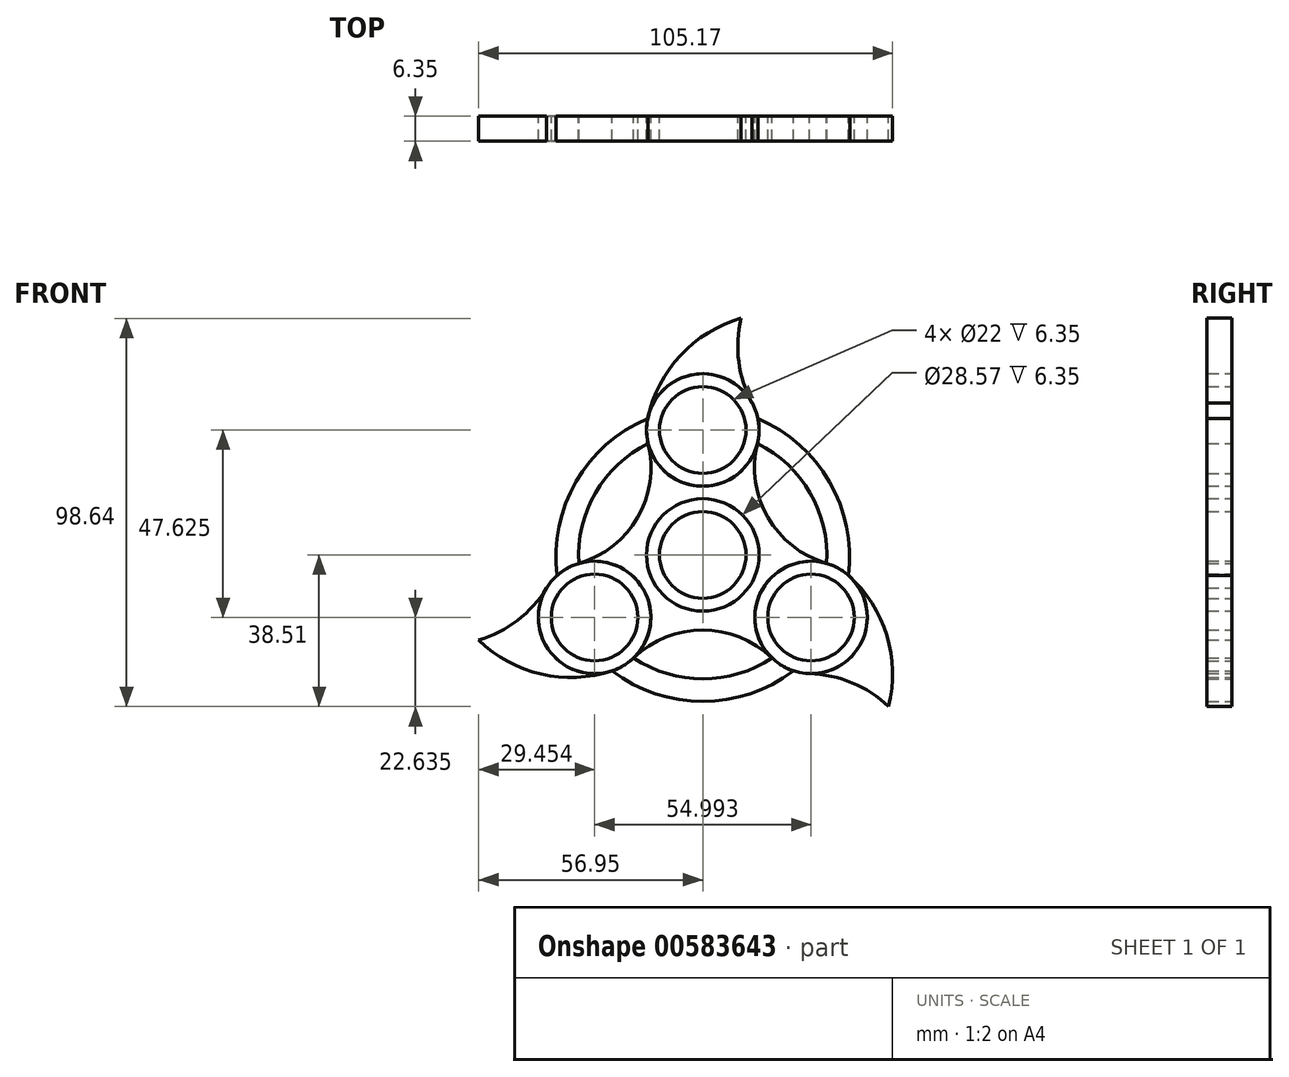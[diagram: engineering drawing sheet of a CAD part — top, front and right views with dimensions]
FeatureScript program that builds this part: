
annotation { "Feature Type Name" : "Feature", "Feature Type Description" : "" }
export const myFeature = defineFeature(function(context is Context, id is Id, definition is map)
    precondition{}
    {
        {
            var Q0;
            Q0=qCreatedBy(makeId("Front.planeOp"),FACE);
            var sketch = newSketch(context, id + "F0", { "sketchPlane" : qUnion([Q0])});
            skCircle(sketch, "E0", {"center": v(0, 0) * mm, "radius": 14.29 * mm});
            skCircle(sketch, "E1", {"center": v(0, 0) * mm, "radius": 11 * mm});
            skCircle(sketch, "E2", {"center": v(0, 31.75) * mm, "radius": 14.29 * mm});
            skCircle(sketch, "E3", {"center": v(0, 31.75) * mm, "radius": 11 * mm});
            skCircle(sketch, "E4.1.0", {"center": v(-27.5, -15.87) * mm, "radius": 11 * mm});
            skCircle(sketch, "E4.1.1", {"center": v(-27.5, -15.87) * mm, "radius": 14.29 * mm});
            skCircle(sketch, "E4.2.0", {"center": v(27.5, -15.88) * mm, "radius": 11 * mm});
            skCircle(sketch, "E4.2.1", {"center": v(27.5, -15.88) * mm, "radius": 14.29 * mm});
            skSolve(sketch);
        }
        {
            var Q0;
            Q0=qCreatedBy(makeId("Front.planeOp"),FACE);
            var sketch = newSketch(context, id + "F1", { "sketchPlane" : qUnion([Q0])});
            skCircle(sketch, "E5.0", {"center": v(0, 31.75) * mm, "radius": 14.29 * mm});
            skCircle(sketch, "E6.0", {"center": v(27.5, -15.88) * mm, "radius": 14.29 * mm});
            skCircle(sketch, "E7.0", {"center": v(-27.5, -15.87) * mm, "radius": 14.29 * mm});
            skCircle(sketch, "E8.0", {"center": v(0, 0) * mm, "radius": 14.29 * mm});
            skArc(sketch, "E9", {"start": v(-31.47, -2.15) * mm, "mid": v(-16.54, 9.55) * mm, "end": v(-13.87, 28.33) * mm});
            skArc(sketch, "E10", {"start": v(13.87, 28.33) * mm, "mid": v(16.54, 9.55) * mm, "end": v(31.47, -2.15) * mm});
            skArc(sketch, "E11", {"start": v(17.6, -26.18) * mm, "mid": v(0, -19.1) * mm, "end": v(-17.6, -26.18) * mm});
            skArc(sketch, "E12", {"start": v(-13.87, 28.33) * mm, "mid": v(-27.28, 15.75) * mm, "end": v(-31.47, -2.15) * mm});
            skArc(sketch, "E13", {"start": v(31.47, -2.15) * mm, "mid": v(27.28, 15.75) * mm, "end": v(13.87, 28.33) * mm});
            skArc(sketch, "E14", {"start": v(-17.6, -26.18) * mm, "mid": v(0, -31.5) * mm, "end": v(17.6, -26.18) * mm});
            skArc(sketch, "E15", {"start": v(-13.98, 34.68) * mm, "mid": v(-32.22, 18.6) * mm, "end": v(-37.02, -5.23) * mm});
            skArc(sketch, "E16", {"start": v(37.02, -5.23) * mm, "mid": v(32.18, 18.63) * mm, "end": v(13.87, 34.68) * mm});
            skArc(sketch, "E17", {"start": v(-23.04, -29.45) * mm, "mid": v(0, -37.2) * mm, "end": v(23.04, -29.45) * mm});
            skSolve(sketch);
        }
        {
            var Q0;
            Q0=qCreatedBy(makeId("Front.planeOp"),FACE);
            var sketch = newSketch(context, id + "F2", { "sketchPlane" : qUnion([Q0])});
            skCircle(sketch, "E18.0", {"center": v(0, 31.75) * mm, "radius": 14.29 * mm});
            skArc(sketch, "E19.0", {"start": v(-13.98, 34.68) * mm, "mid": v(-32.22, 18.6) * mm, "end": v(-37.02, -5.23) * mm});
            skCircle(sketch, "E20.0", {"center": v(-27.5, -15.87) * mm, "radius": 14.29 * mm});
            skArc(sketch, "E21.0", {"start": v(-23.04, -29.45) * mm, "mid": v(0, -37.2) * mm, "end": v(23.04, -29.45) * mm});
            skCircle(sketch, "E22.0", {"center": v(27.5, -15.88) * mm, "radius": 14.29 * mm});
            skArc(sketch, "E23.0", {"start": v(37.02, -5.23) * mm, "mid": v(32.18, 18.63) * mm, "end": v(13.87, 34.68) * mm});
            skPoint(sketch, "E24.endSnap0", {"position": v(1.06, 56.27) * mm});
            skArc(sketch, "E25", {"start": v(9.75, 60.13) * mm, "mid": v(-5.67, 50.72) * mm, "end": v(-13.98, 34.68) * mm});
            skArc(sketch, "E26", {"start": v(9.75, 60.13) * mm, "mid": v(9.14, 49.1) * mm, "end": v(12.55, 38.58) * mm});
            skArc(sketch, "E27.1.0", {"start": v(-56.95, -21.62) * mm, "mid": v(-41.09, -30.27) * mm, "end": v(-23.04, -29.45) * mm});
            skArc(sketch, "E27.1.1", {"start": v(-56.95, -21.62) * mm, "mid": v(-47.09, -16.64) * mm, "end": v(-39.69, -8.43) * mm});
            skArc(sketch, "E27.2.0", {"start": v(47.2, -38.51) * mm, "mid": v(46.76, -20.45) * mm, "end": v(37.02, -5.23) * mm});
            skArc(sketch, "E27.2.1", {"start": v(47.2, -38.51) * mm, "mid": v(37.95, -32.46) * mm, "end": v(27.14, -30.16) * mm});
            skPoint(sketch, "E27.center", {"position": v(0, 0) * mm});
            skSolve(sketch);
        }
        {
            var Q0;
            {var subQ0=sQuery(id+"F2.wireOp",EDGE,"E25");Q0=makeQuery(id+"F2.imprint","IMPRINT",FACE,{"disambiguationData":[TD([[makeQuery(id+"F2.imprint","IMPRINT",EDGE,{"derivedFrom":subQ0}),1.0]])]});}
            var Q1;
            {var subQ0=sQuery(id+"F1.wireOp",EDGE,"E13");Q1=makeQuery(id+"F1.imprint","IMPRINT",FACE,{"disambiguationData":[TD([[makeQuery(id+"F1.imprint","IMPRINT",EDGE,{"derivedFrom":subQ0}),-1.0]])]});}
            var Q2;
            {var subQ0=sQuery(id+"F1.wireOp",EDGE,"E14");Q2=makeQuery(id+"F1.imprint","IMPRINT",FACE,{"disambiguationData":[TD([[makeQuery(id+"F1.imprint","IMPRINT",EDGE,{"derivedFrom":subQ0}),-1.0]])]});}
            var Q3;
            {var subQ0=sQuery(id+"F2.wireOp",EDGE,"E27.1.0");Q3=makeQuery(id+"F2.imprint","IMPRINT",FACE,{"disambiguationData":[TD([[makeQuery(id+"F2.imprint","IMPRINT",EDGE,{"derivedFrom":subQ0}),1.0]])]});}
            var Q4;
            {var subQ0=sQuery(id+"F1.wireOp",EDGE,"E12");Q4=makeQuery(id+"F1.imprint","IMPRINT",FACE,{"disambiguationData":[TD([[makeQuery(id+"F1.imprint","IMPRINT",EDGE,{"derivedFrom":subQ0}),-1.0]])]});}
            var Q5;
            Q5=makeQuery(id+"F1.imprint","IMPRINT",FACE,{"disambiguationData":[TD([[makeQuery(id+"F1.imprint","IMPRINT",EDGE,{"derivedFrom":sQuery(id+"F1.wireOp",EDGE,"E8.0")}),-1.0]])]});
            var Q6;
            Q6=makeQuery(id+"F0.imprint","IMPRINT",FACE,{"disambiguationData":[TD([[makeQuery(id+"F0.imprint","IMPRINT",EDGE,{"derivedFrom":sQuery(id+"F0.wireOp",EDGE,"E0")}),1.0]])]});
            var Q7;
            Q7=makeQuery(id+"F0.imprint","IMPRINT",FACE,{"disambiguationData":[TD([[makeQuery(id+"F0.imprint","IMPRINT",EDGE,{"derivedFrom":sQuery(id+"F0.wireOp",EDGE,"E4.1.0")}),-1.0]])]});
            var Q8;
            Q8=makeQuery(id+"F0.imprint","IMPRINT",FACE,{"disambiguationData":[TD([[makeQuery(id+"F0.imprint","IMPRINT",EDGE,{"derivedFrom":sQuery(id+"F0.wireOp",EDGE,"E4.2.0")}),-1.0]])]});
            var Q9;
            Q9=makeQuery(id+"F0.imprint","IMPRINT",FACE,{"disambiguationData":[TD([[makeQuery(id+"F0.imprint","IMPRINT",EDGE,{"derivedFrom":sQuery(id+"F0.wireOp",EDGE,"E2")}),1.0]])]});
            var Q10;
            {var subQ0=sQuery(id+"F2.wireOp",EDGE,"E27.2.0");Q10=makeQuery(id+"F2.imprint","IMPRINT",FACE,{"disambiguationData":[TD([[makeQuery(id+"F2.imprint","IMPRINT",EDGE,{"derivedFrom":subQ0}),1.0]])]});}
            extrude(context, id + "F3", {"entities" : qUnion([Q0, Q1, Q2, Q3, Q4, Q5, Q6, Q7, Q8, Q9, Q10]), "depth" : 6.35 * mm, "offsetDistance" : 25.4 * mm});
        }
    });
